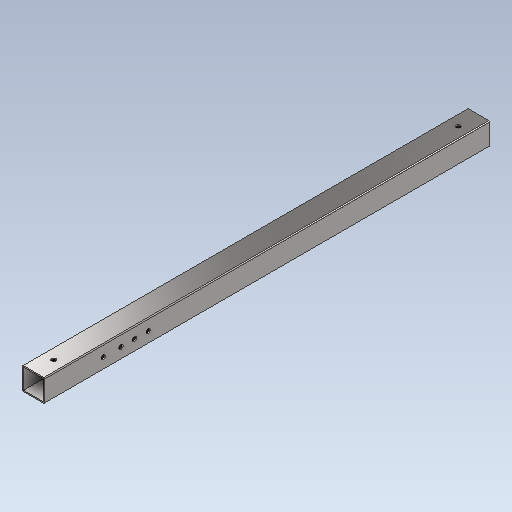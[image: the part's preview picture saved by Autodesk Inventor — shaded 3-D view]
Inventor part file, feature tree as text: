
AUTODESK INVENTOR PART (.ipt)
format: ipt  version: 2021 (Build 250183000, 183)  size: 189,440 bytes
history: native  units: mm
features: sketch x4, hole x3, extrude x1, fillet x1
ambient origin geometry x8: Origin, YZ Plane, XZ Plane, XY Plane, X Axis, Y Axis, Z Axis, Center Point
bodies: Solid1 (feature_tree)
feature tree (9):
  sketch  "Sketch1"  dims[d0=50.0mm d1=50.0mm d2=25.0mm]
  extrude  "Extrusion1"  Depth=50.0mm
  fillet  "Fillet1"  Radius=25.0mm
  hole  "endHoles"  [1 undecoded]
  hole  "clampHoles"  [1 undecoded]
  hole  "Hole3"  [1 undecoded]
  sketch  "Sketch2"  dims[d3=25.0mm d4=2.5mm]
  sketch  "Sketch3"  dims[d5=990.0mm d6=0.0mm]
  sketch  "Sketch4"  dims[d7=2.0mm d8=45.0mm d9=0.0mm d10=45.0mm d11=0.0mm d12=10.0mm d13=6.0mm d14=4.0mm d15=2.0mm d16=90.0deg d17=8.0mm d18=0.0mm d19=860.0mm d20=760.0mm d21=0.0mm d22=0.0mm d23=10.0mm d24=6.0mm d25=4.0mm d26=2.0mm d27=90.0deg d28=8.0mm d29=20.594885mm d30=30.0mm d32=39.6mm d33=10.0mm d34=6.0mm d35=4.0mm d36=2.0mm d37=90.0deg d38=8.0mm d39=20.594885mm]
note: 3 required parameter values undecoded (feature->parameter linkage not recoverable at this tier; creation-order binding heuristic only, values carry confidence <= 0.55)
